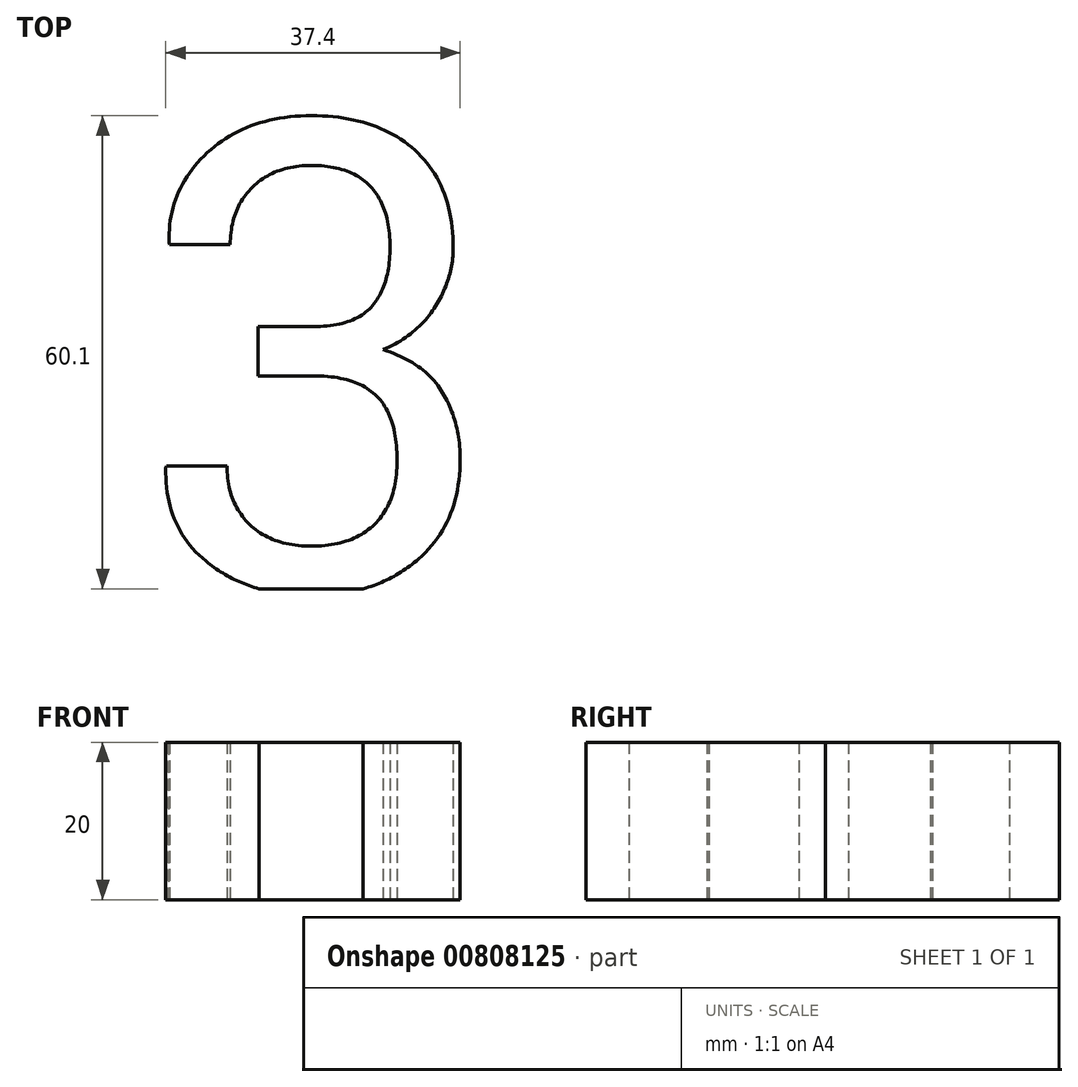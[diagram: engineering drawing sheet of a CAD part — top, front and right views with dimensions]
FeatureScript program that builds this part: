
annotation { "Feature Type Name" : "Feature", "Feature Type Description" : "" }
export const myFeature = defineFeature(function(context is Context, id is Id, definition is map)
    precondition{}
    {
        {
            var Q0;
            Q0=qCreatedBy(makeId("Top.planeOp"),FACE);
            var sketch = newSketch(context, id + "F0", { "sketchPlane" : qUnion([Q0])});
            skText(sketch, "E0", { "text": "3", "fontName": "RobotoSlab-Regular.ttf"});
            const initialGuessF0  = {"E0": [0, 0, 1, 0, 0.06]};
            skSetInitialGuess(sketch, initialGuessF0);
            skSolve(sketch);
        }
        {
            var Q0;
            Q0 = qSketchRegion(id + "F0", true);
            extrude(context, id + "F1", {"entities" : qUnion([Q0]), "depth" : 20 * mm, "offsetDistance" : 25 * mm});
        }
        {
            var Q0;
            Q0=makeQuery(id+"F1.opExtrude","CAP_FACE",FACE,{"disambiguationData":[OSD([sQuery(id+"F0.wireOp",EDGE,"E0.sketch_text.stroke-0"),sQuery(id+"F0.wireOp",EDGE,"E0.sketch_text.stroke-1"),sQuery(id+"F0.wireOp",EDGE,"E0.sketch_text.stroke-2"),sQuery(id+"F0.wireOp",EDGE,"E0.sketch_text.stroke-3"),sQuery(id+"F0.wireOp",EDGE,"E0.sketch_text.stroke-4"),sQuery(id+"F0.wireOp",EDGE,"E0.sketch_text.stroke-5"),sQuery(id+"F0.wireOp",EDGE,"E0.sketch_text.stroke-6"),sQuery(id+"F0.wireOp",EDGE,"E0.sketch_text.stroke-7"),sQuery(id+"F0.wireOp",EDGE,"E0.sketch_text.stroke-8"),sQuery(id+"F0.wireOp",EDGE,"E0.sketch_text.stroke-9"),sQuery(id+"F0.wireOp",EDGE,"E0.sketch_text.stroke-10"),sQuery(id+"F0.wireOp",EDGE,"E0.sketch_text.stroke-11"),sQuery(id+"F0.wireOp",EDGE,"E0.sketch_text.stroke-12"),sQuery(id+"F0.wireOp",EDGE,"E0.sketch_text.stroke-13"),sQuery(id+"F0.wireOp",EDGE,"E0.sketch_text.stroke-14"),sQuery(id+"F0.wireOp",EDGE,"E0.sketch_text.stroke-15"),sQuery(id+"F0.wireOp",EDGE,"E0.sketch_text.stroke-16"),sQuery(id+"F0.wireOp",EDGE,"E0.sketch_text.stroke-17"),sQuery(id+"F0.wireOp",EDGE,"E0.sketch_text.stroke-18"),sQuery(id+"F0.wireOp",EDGE,"E0.sketch_text.stroke-19"),sQuery(id+"F0.wireOp",EDGE,"E0.sketch_text.stroke-20"),sQuery(id+"F0.wireOp",EDGE,"E0.sketch_text.stroke-21"),sQuery(id+"F0.wireOp",EDGE,"E0.sketch_text.stroke-22"),sQuery(id+"F0.wireOp",EDGE,"E0.sketch_text.stroke-23"),sQuery(id+"F0.wireOp",EDGE,"E0.sketch_text.stroke-24"),sQuery(id+"F0.wireOp",EDGE,"E0.sketch_text.stroke-25"),sQuery(id+"F0.wireOp",EDGE,"E0.sketch_text.stroke-26"),sQuery(id+"F0.wireOp",EDGE,"E0.sketch_text.stroke-27"),sQuery(id+"F0.wireOp",EDGE,"E0.sketch_text.stroke-28"),sQuery(id+"F0.wireOp",EDGE,"E0.sketch_text.stroke-29"),sQuery(id+"F0.wireOp",EDGE,"E0.sketch_text.stroke-30")])],"isStart":false});
            var sketch = newSketch(context, id + "F2", { "sketchPlane" : qUnion([Q0])});
            skLineSegment(sketch, "E1.bottom", {"start": v(0, 0) * mm, "end": v(44.06, 0) * mm});
            skLineSegment(sketch, "E1.top", {"start": v(0, -10.94) * mm, "end": v(44.06, -10.94) * mm});
            skLineSegment(sketch, "E1.left", {"start": v(0, 0) * mm, "end": v(0, -10.94) * mm});
            skLineSegment(sketch, "E1.right", {"start": v(44.06, 0) * mm, "end": v(44.06, -10.94) * mm});
            skSolve(sketch);
        }
        {
            var Q0;
            Q0 = qSketchRegion(id + "F2", true);
            extrude(context, id + "F3", {"entities" : qUnion([Q0]), "operationType" : NewBodyOperationType.REMOVE, "oppositeDirection" : true, "depth" : 25 * mm, "offsetDistance" : 25 * mm});
        }
    });
